# Revit family: 304_8dddfd2dcc6a4d7fb22ae320b8647c
name_source: partatom
category: Pipe Accessories
units: mm (PartAtom-declared; Revit-internal decimal feet)

## family parameters
Always vertical = Yes
Cut with Voids When Loaded = No
Part Type = Valve - Breaks Into
Round Connector Dimension = Use Diameter
Shared = No
Work Plane-Based = No

## types (2) — shared parameters
A = 30.00°
Description = Pressure independent control valve
H1 = 62 mm  [stored 0.203412 ft]
H2 = 15 mm  [stored 0.0492126 ft]
H3 = 35 mm  [stored 0.114829 ft]
H31 = 10 mm  [stored 0.0328084 ft]
H4 = 60 mm  [stored 0.19685 ft]
H5 = 30 mm  [stored 0.0984252 ft]
H51 = 40 mm  [stored 0.131234 ft]
H7 = 86 mm
L1 = 35 mm  [stored 0.114829 ft]
L1__ve = -35 mm  [stored -0.114829 ft]
L2 = 68 mm  [stored 0.223097 ft]
L2D = 138 mm
L2D_Min = 3048 mm  [stored 10 ft]
L3 = 13 mm
L4 = 90 mm  [stored 0.295276 ft]
L5 = 29 mm  [stored 0.0951444 ft]
L6 = 10 mm  [stored 0.0328084 ft]
LL = 69 mm  [stored 0.226378 ft]
Manufacturer = Frese A/S
PLG0 = Yes
QmdConnectorList = 301;D;302;D
R3 = 45 mm  [stored 0.147638 ft]
R4 = 34 mm  [stored 0.111549 ft]
R5 = 5 mm  [stored 0.0164042 ft]
R6 = 22 mm  [stored 0.0721785 ft]
R7 = 7 mm  [stored 0.0229659 ft]
R9 = 8 mm  [stored 0.0262467 ft]
S1 = 6 mm  [stored 0.019685 ft]
S2 = 14 mm  [stored 0.0459318 ft]
S3 = 40 mm  [stored 0.131234 ft]
URL = https://www.frese.eu
W2D = 40 mm  [stored 0.131234 ft]
magiPartTypeId = 304
magiProductFamilyId = 8dddfd2dcc6a4d7fb22ae320b8647c

## per-type parameters (varying)
| type | CenSd_R1_6 | D | H6 | H6__ve | R1 | R2 | X | Z | magiProductId |
| Frese OPTIMA Compact F/F PT Plug and Spring return actuator DOWN DN40 | 28 mm | 40 mm | 74 mm  [stored 0.242782 ft] | -74 mm  [stored -0.242782 ft] | 32 mm  [stored 0.104987 ft] | 27 mm  [stored 0.0885827 ft] | 15 mm  [stored 0.0492126 ft] | 7 mm  [stored 0.0229659 ft] | bb3a4bde3d1344299bff1186d743f5 |
| Frese OPTIMA Compact F/F PT Plug and Spring return actuator DOWN DN50 | 35 mm  [stored 0.114829 ft] | 50 mm | 82 mm  [stored 0.269029 ft] | -82 mm  [stored -0.269029 ft] | 40 mm  [stored 0.131234 ft] | 34 mm  [stored 0.111549 ft] | 19 mm  [stored 0.062336 ft] | 0 mm  [stored 0 ft] | a33442609bdf4937a369fef52866bf |

note: column(s) folded — value = type name in every type: MC Product Code

note: [stored X ft] marks values corroborated as IEEE doubles in the binary element streams (Revit-internal decimal feet)

## geometry (parser evidence)
native form markers: Sweep x1
no freeform markers — native parametric forms only
